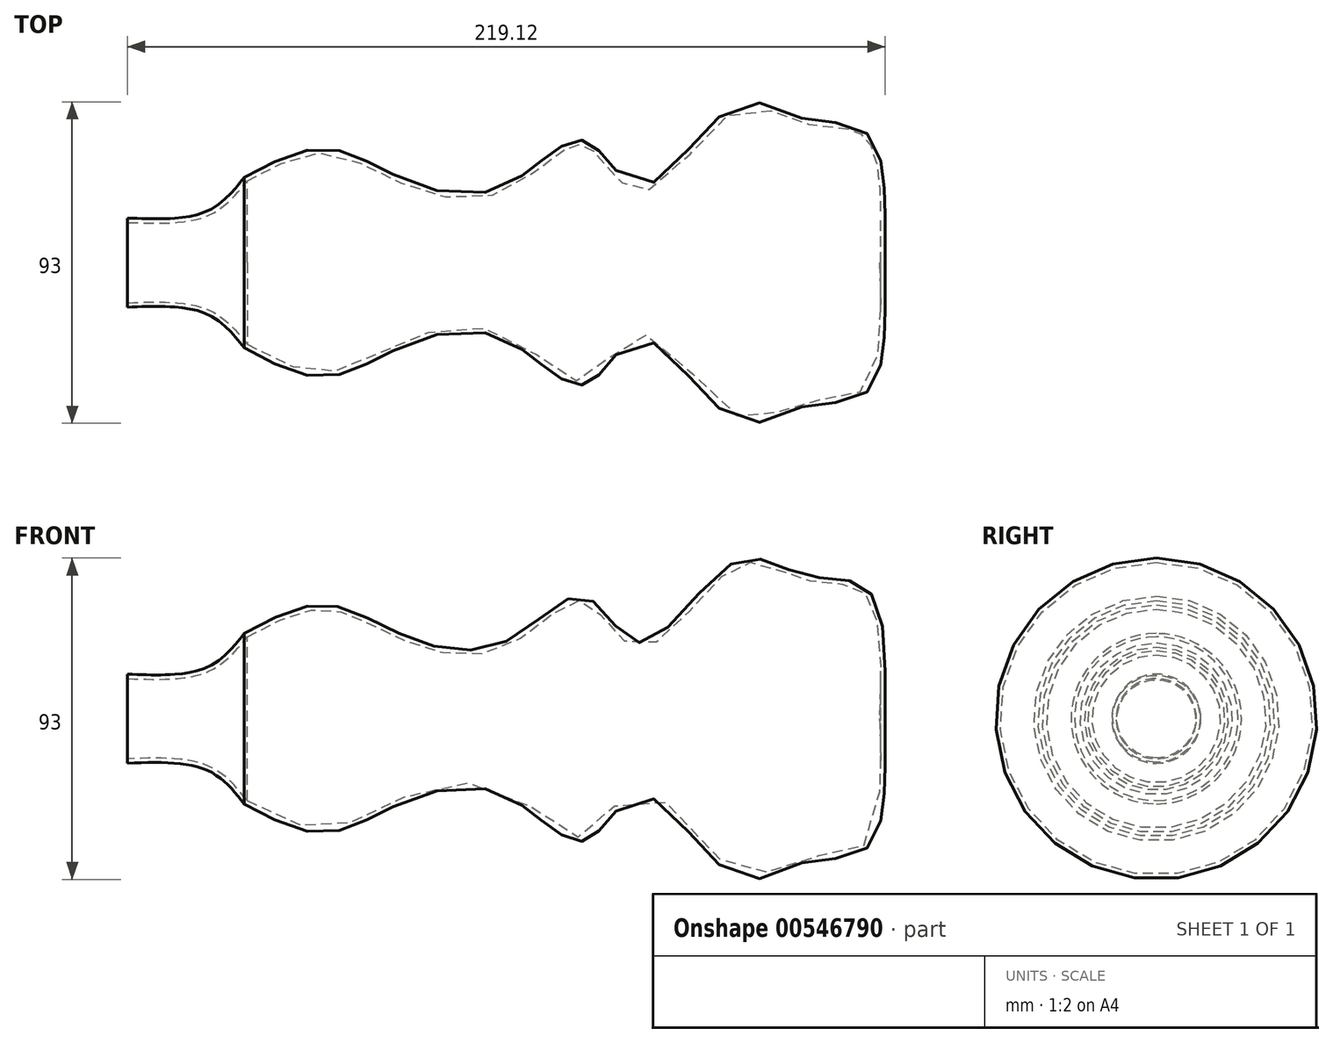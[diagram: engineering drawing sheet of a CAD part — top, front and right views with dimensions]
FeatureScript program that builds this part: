
annotation { "Feature Type Name" : "Feature", "Feature Type Description" : "" }
export const myFeature = defineFeature(function(context is Context, id is Id, definition is map)
    precondition{}
    {
        {
            var Q0;
            Q0=qCreatedBy(makeId("Front.planeOp"),FACE);
            var sketch = newSketch(context, id + "F0", { "sketchPlane" : qUnion([Q0])});
            skFitSpline(sketch, "E0", {"points": [v(-54.6, 24.65) * mm, v(-31.1, 32.99) * mm, v(-7.96, 23.89) * mm, v(21.23, 22.37) * mm, v(43.99, 35.27) * mm, v(59.91, 22) * mm, v(87.6, 45.5) * mm, v(106.93, 41.71) * mm, v(125.51, 37.54) * mm, v(130.44, 0) * mm], "startDerivative": vector(220.48, 120.58) * mm, "endDerivative": vector(-12.53, -360.1) * mm});
            skFitSpline(sketch, "E1", {"points": [v(-54.6, 24.65) * mm, v(-65.6, 14.79) * mm, v(-88.35, 12.9) * mm], "startDerivative": vector(-21.02, -26.28) * mm, "endDerivative": vector(-45.6, 1.76) * mm});
            skLineSegment(sketch, "E2", {"start": v(145.61, 0) * mm, "end": v(-117.17, 0) * mm});
            skLineSegment(sketch, "E3", {"start": v(-88.35, 12.9) * mm, "end": v(-88.35, 0) * mm});
            skSolve(sketch);
        }
        {
            var Q0;
            {var subQ0=sQuery(id+"F0.wireOp",EDGE,"E0");Q0=makeQuery(id+"F0.imprint","IMPRINT",FACE,{"disambiguationData":[TD([[makeQuery(id+"F0.imprint","IMPRINT",EDGE,{"derivedFrom":subQ0}),-1.0]])]});}
            var Q1;
            Q1=sQuery(id+"F0.wireOp",EDGE,"E2");
            revolve(context, id + "F1", {"entities" : qUnion([Q0]), "axis" : qUnion([Q1]), "revolveType" : RevolveType.FULL});
        }
        {
            var Q0;
            Q0=makeQuery(id+"F1.opRevolve","SWEPT_FACE",FACE,{"disambiguationData":[OSD([sQuery(id+"F0.wireOp",EDGE,"E3")])]});
            shell(context, id + "F2", {"entities" : qUnion([Q0]), "thickness" : 1.27 * mm});
        }
    });
